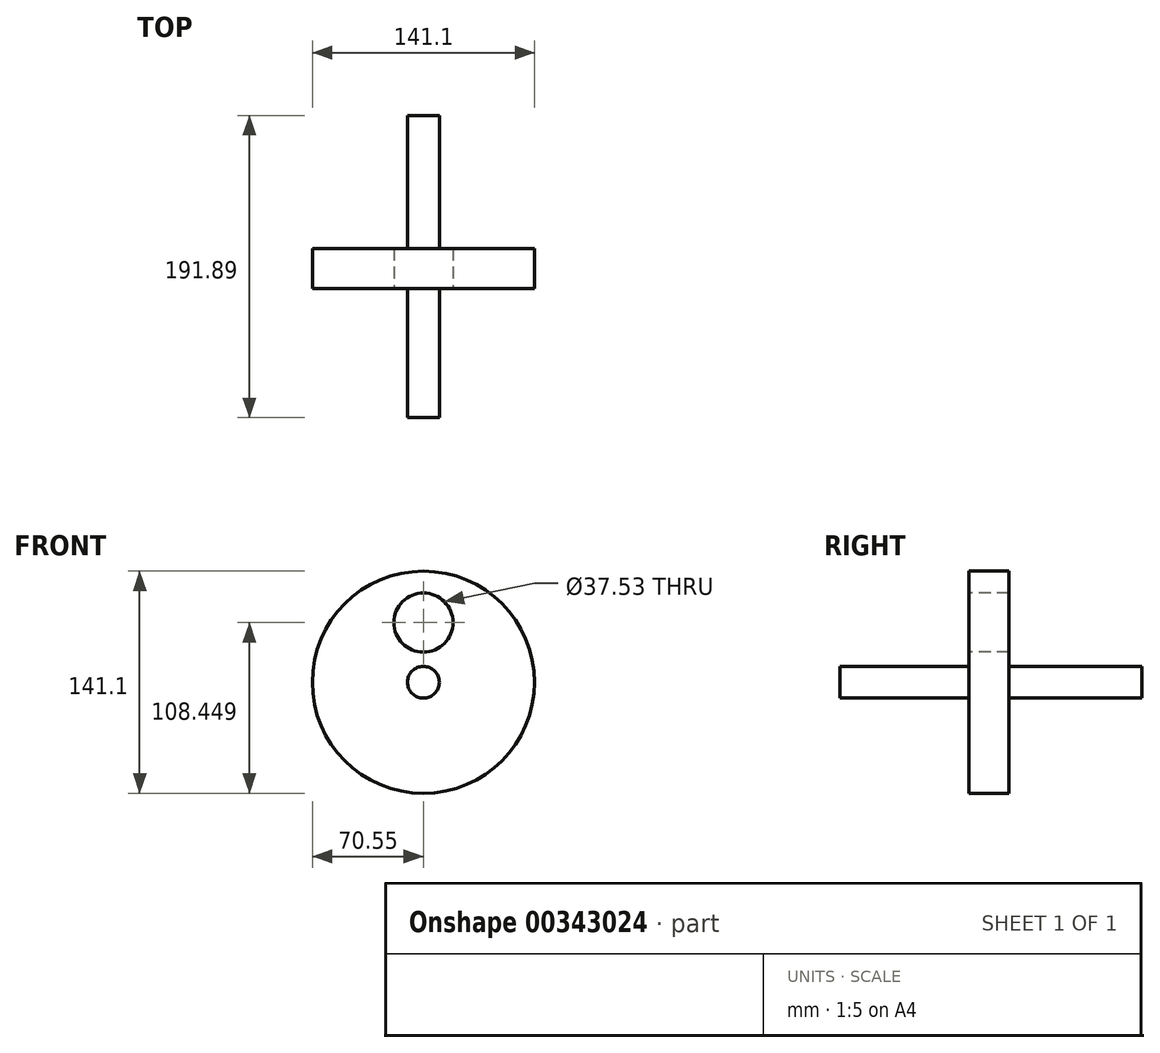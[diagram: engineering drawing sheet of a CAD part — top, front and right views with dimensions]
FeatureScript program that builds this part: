
annotation { "Feature Type Name" : "Feature", "Feature Type Description" : "" }
export const myFeature = defineFeature(function(context is Context, id is Id, definition is map)
    precondition{}
    {
        {
            var Q0;
            Q0=qCreatedBy(makeId("Front.planeOp"),FACE);
            var sketch = newSketch(context, id + "F0", { "sketchPlane" : qUnion([Q0])});
            skCircle(sketch, "E0", {"center": v(0, 0) * mm, "radius": 70.55 * mm});
            skSolve(sketch);
        }
        {
            var Q0;
            Q0 = qSketchRegion(id + "F0", true);
            extrude(context, id + "F1", {"entities" : qUnion([Q0]), "depth" : 25.4 * mm});
        }
        {
            var Q0;
            Q0=makeQuery(id+"F1.opExtrude","CAP_FACE",FACE,{"disambiguationData":[OSD([sQuery(id+"F0.wireOp",EDGE,"E0")])],"isStart":false});
            var sketch = newSketch(context, id + "F2", { "sketchPlane" : qUnion([Q0])});
            skCircle(sketch, "E1", {"center": v(0, 37.9) * mm, "radius": 18.76 * mm});
            skSolve(sketch);
        }
        {
            var Q0;
            Q0 = qSketchRegion(id + "F2", true);
            extrude(context, id + "F3", {"entities" : qUnion([Q0]), "operationType" : NewBodyOperationType.REMOVE, "oppositeDirection" : true, "depth" : 61.6 * mm});
        }
        {
            var Q0;
            Q0=makeQuery(id+"F2.imprint","IMPRINT",FACE,{"disambiguationData":[TD([[makeQuery(id+"F2.imprint","IMPRINT",EDGE,{"derivedFrom":sQuery(id+"F2.wireOp",EDGE,"E1")}),-1.0]])]});
            var sketch = newSketch(context, id + "F4", { "sketchPlane" : qUnion([Q0])});
            skCircle(sketch, "E2", {"center": v(0, 0) * mm, "radius": 10.07 * mm});
            skSolve(sketch);
        }
        {
            var Q0;
            Q0 = qSketchRegion(id + "F4", true);
            extrude(context, id + "F5", {"entities" : qUnion([Q0]), "operationType" : NewBodyOperationType.ADD, "depth" : 81.97 * mm, "hasSecondDirection" : true, "secondDirectionOppositeDirection" : true, "secondDirectionDepth" : 109.92 * mm});
        }
    });
